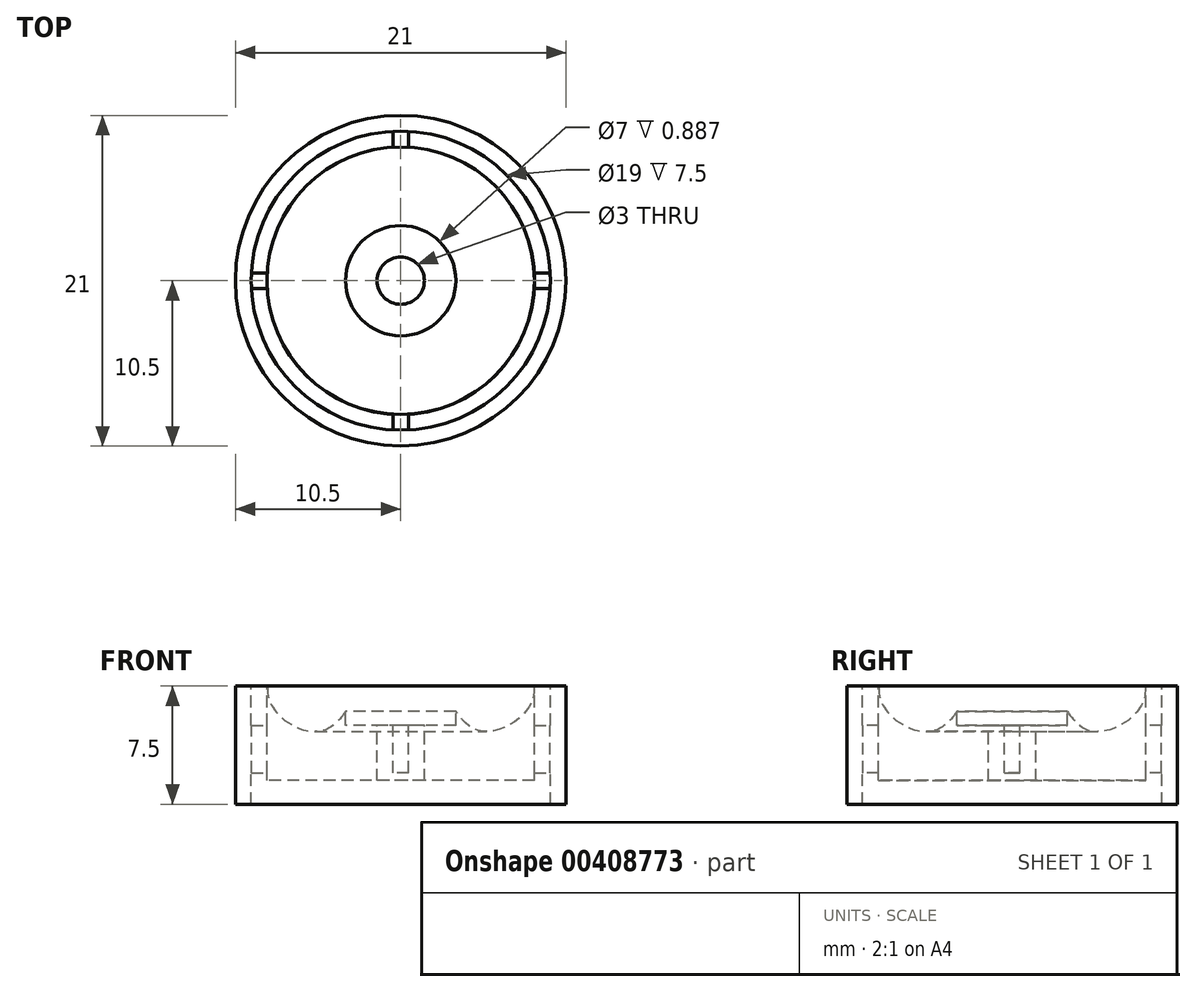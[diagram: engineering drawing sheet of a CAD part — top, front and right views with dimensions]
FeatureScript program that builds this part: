
annotation { "Feature Type Name" : "Feature", "Feature Type Description" : "" }
export const myFeature = defineFeature(function(context is Context, id is Id, definition is map)
    precondition{}
    {
        {
            var Q0;
            Q0=qCreatedBy(makeId("Top.planeOp"),FACE);
            var sketch = newSketch(context, id + "F0", { "sketchPlane" : qUnion([Q0])});
            skCircle(sketch, "E0", {"center": v(0, 0) * mm, "radius": 10.5 * mm});
            skCircle(sketch, "E1", {"center": v(0, 0) * mm, "radius": 9.5 * mm});
            skCircle(sketch, "E2", {"center": v(0, 0) * mm, "radius": 8.5 * mm});
            skCircle(sketch, "E3", {"center": v(0, 0) * mm, "radius": 3.5 * mm});
            skCircle(sketch, "E4", {"center": v(0, 0) * mm, "radius": 1.5 * mm});
            skSolve(sketch);
        }
        {
            var Q0;
            Q0=makeQuery(id+"F0.imprint","IMPRINT",FACE,{"disambiguationData":[TD([[makeQuery(id+"F0.imprint","IMPRINT",EDGE,{"derivedFrom":sQuery(id+"F0.wireOp",EDGE,"E0")}),1.0]])]});
            var Q1;
            Q1=sQuery(id+"F0.wireOp",EDGE,"E0");
            var Q2;
            Q2=sQuery(id+"F0.wireOp",EDGE,"E1");
            extrude(context, id + "F1", {"entities" : qUnion([Q0]), "surfaceEntities" : qUnion([Q1, Q2]), "oppositeDirection" : true, "depth" : 7.5 * mm});
        }
        {
            var Q0;
            Q0=makeQuery(id+"F0.imprint","IMPRINT",FACE,{"disambiguationData":[TD([[makeQuery(id+"F0.imprint","IMPRINT",EDGE,{"derivedFrom":sQuery(id+"F0.wireOp",EDGE,"E2")}),1.0]])]});
            extrude(context, id + "F2", {"entities" : qUnion([Q0]), "oppositeDirection" : true, "depth" : 6 * mm});
        }
        {
            var Q0;
            Q0=qCreatedBy(makeId("Front.planeOp"),FACE);
            var sketch = newSketch(context, id + "F3", { "sketchPlane" : qUnion([Q0])});
            skLineSegment(sketch, "E5", {"start": v(0, 7.42) * mm, "end": v(0, -7.28) * mm, "construction": true});
            skFitSpline(sketch, "E6", {"points": [v(-8.5, 0.03) * mm, v(-8.38, -0.82) * mm, v(-7.18, -2.3) * mm, v(-4.94, -2.83) * mm, v(-3.5, -1.6) * mm, v(-2.36, -0.56) * mm, v(0, -0.18) * mm], "startDerivative": vector(1.52, -5.71) * mm, "endDerivative": vector(8.1, 4.86) * mm});
            skLineSegment(sketch, "E7", {"start": v(0, -0.18) * mm, "end": v(0, 0.07) * mm});
            skLineSegment(sketch, "E8", {"start": v(0, 0.07) * mm, "end": v(-8.5, 0.03) * mm});
            skSolve(sketch);
        }
        {
            var Q0;
            Q0=qCreatedBy(makeId("Top.planeOp"),FACE);
            cPlane(context, id + "F4", {"entities" : qUnion([Q0]), "cplaneType" : CPlaneType.OFFSET, "offset" : 2.5 * mm, "oppositeDirection" : true, "width" : 150 * mm, "height" : 150 * mm});
        }
        {
            var Q0;
            Q0=qCreatedBy(id+"F4.planeOp",FACE);
            var sketch = newSketch(context, id + "F5", { "sketchPlane" : qUnion([Q0])});
            skLineSegment(sketch, "E9.bottom", {"start": v(-9.5, 0.5) * mm, "end": v(9.5, 0.5) * mm});
            skLineSegment(sketch, "E9.top", {"start": v(-9.5, -0.5) * mm, "end": v(9.5, -0.5) * mm});
            skLineSegment(sketch, "E9.left", {"start": v(-9.5, 0.5) * mm, "end": v(-9.5, -0.5) * mm});
            skLineSegment(sketch, "E9.right", {"start": v(9.5, 0.5) * mm, "end": v(9.5, -0.5) * mm});
            skPoint(sketch, "E9.middle", {"position": v(0, 0) * mm});
            skLineSegment(sketch, "E10.bottom", {"start": v(-0.5, 9.5) * mm, "end": v(0.5, 9.5) * mm});
            skLineSegment(sketch, "E10.top", {"start": v(-0.5, -9.5) * mm, "end": v(0.5, -9.5) * mm});
            skLineSegment(sketch, "E10.left", {"start": v(-0.5, 9.5) * mm, "end": v(-0.5, -9.5) * mm});
            skLineSegment(sketch, "E10.right", {"start": v(0.5, 9.5) * mm, "end": v(0.5, -9.5) * mm});
            skSolve(sketch);
        }
        {
            var Q0;
            Q0 = qSketchRegion(id + "F5", true);
            extrude(context, id + "F6", {"entities" : qUnion([Q0]), "operationType" : NewBodyOperationType.ADD, "oppositeDirection" : true, "depth" : 3 * mm});
        }
        {
            var Q0;
            Q0=makeQuery(id+"F3.imprint","IMPRINT",FACE,{"disambiguationData":[TD([[makeQuery(id+"F3.imprint","IMPRINT",EDGE,{"derivedFrom":sQuery(id+"F3.wireOp",EDGE,"E6")}),1.0]])]});
            var Q1;
            Q1=sQuery(id+"F3.wireOp",EDGE,"E5");
            revolve(context, id + "F7", {"operationType" : NewBodyOperationType.REMOVE, "entities" : qUnion([Q0]), "axis" : qUnion([Q1]), "revolveType" : RevolveType.FULL});
        }
        {
            var Q0;
            Q0=qCreatedBy(id+"F4.planeOp",FACE);
            var sketch = newSketch(context, id + "F8", { "sketchPlane" : qUnion([Q0])});
            skCircle(sketch, "E11", {"center": v(0, 0) * mm, "radius": 1.5 * mm});
            skCircle(sketch, "E12", {"center": v(0, 0) * mm, "radius": 3.5 * mm});
            skSolve(sketch);
        }
        {
            var Q0;
            Q0 = qSketchRegion(id + "F8", true);
            var Q1;
            Q1=makeQuery(id+"F2.opExtrude","CAP_FACE",FACE,{"disambiguationData":[OSD([sQuery(id+"F0.wireOp",EDGE,"E2"),sQuery(id+"F0.wireOp",EDGE,"E3")])],"isStart":false});
            extrude(context, id + "F9", {"entities" : qUnion([Q0]), "operationType" : NewBodyOperationType.ADD, "endBound" : BoundingType.UP_TO_SURFACE, "oppositeDirection" : true, "endBoundEntityFace" : qUnion([Q1]), "depth" : 3.5 * mm});
        }
        {
            var Q0;
            Q0=makeQuery(id+"F0.imprint","IMPRINT",FACE,{"disambiguationData":[TD([[makeQuery(id+"F0.imprint","IMPRINT",EDGE,{"derivedFrom":sQuery(id+"F0.wireOp",EDGE,"E4")}),1.0]])]});
            var Q1;
            Q1=sQuery(id+"F0.wireOp",EDGE,"E4");
            var Q2;
            Q2=makeQuery(id+"F2.opExtrude","CAP_FACE",FACE,{"disambiguationData":[OSD([sQuery(id+"F0.wireOp",EDGE,"E2"),sQuery(id+"F0.wireOp",EDGE,"E3")])],"isStart":false});
            extrude(context, id + "F10", {"entities" : qUnion([Q0]), "operationType" : NewBodyOperationType.REMOVE, "surfaceEntities" : qUnion([Q1]), "endBound" : BoundingType.UP_TO_SURFACE, "oppositeDirection" : true, "endBoundEntityFace" : qUnion([Q2]), "depth" : 25 * mm});
        }
    });
